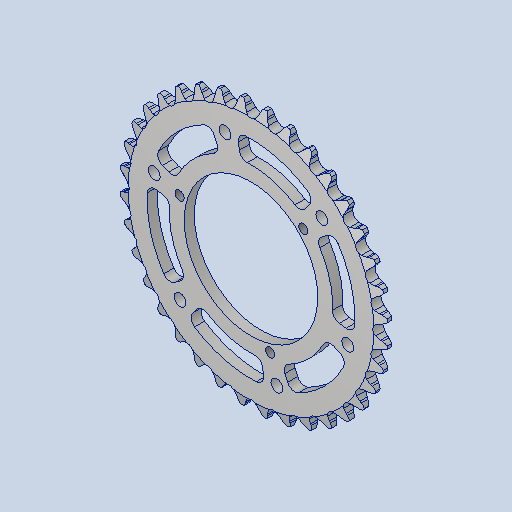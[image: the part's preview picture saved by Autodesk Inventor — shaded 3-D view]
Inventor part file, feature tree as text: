
AUTODESK INVENTOR PART (.ipt)
format: ipt  version: 2022.3 (Build 263350000, 350)  size: 1,099,776 bytes
history: native  units: in
note: dims shown in document units (in); Inventor stores cm internally (conversion verified against a paired STEP export)
features: sketch x4, extrude x2, hole x2, projected_geometry x2, fillet x1, pattern_circular x1, boolean_combine x1
ambient origin geometry x8: Origin, YZ Plane, XZ Plane, XY Plane, X Axis, Y Axis, Z Axis, Center Point
bodies: Solid1 (feature_tree)
feature tree (13):
  extrude  "Extrusion1"  TaperAngle=0.0deg  [1 undecoded]
  hole  "Hole1"  [1 undecoded]
  hole  "Hole2"  [1 undecoded]
  extrude  "Extrusion2"  Depth=0.13in TaperAngle=360.0deg
  fillet  "Fillet1"  Radius=4.0in
  pattern_circular  "Circular Pattern2"  [2 undecoded]
  sketch  "Sketch1"  dims[d0=2.25in d1=0.0in d2=0.0in]
  sketch  "Sketch2"  dims[d3=2.3622in d5=360.0deg d7=3.375in]
  sketch  "Sketch3"  dims[d8=0.201in d9=0.38in d10=0.385in d11=0.25in d12=0.563in d13=1.0in d14=0.8108in d15=0.24in]
  projected_geometry  "Projected Loop1"
  sketch  "Sketch5"  dims[d16=0.0in d17=1.1811in d19=360.0deg d21=0.156in d22=0.38in d23=0.385in d24=0.25in d25=0.563in d26=1.0in d27=0.8108in d28=4.0in d29=0.25in d30=3.5in d31=0.438in d32=0.25in d33=0.0in d34=0.0in d38=0.13in d39=2.3622in d40=2.4737in d18=0.15in d20=0.375in]
  projected_geometry  "Projected Loop2"
  boolean_combine  "Combine1"
note: 5 required parameter values undecoded (feature->parameter linkage not recoverable at this tier; creation-order binding heuristic only, values carry confidence <= 0.55)
